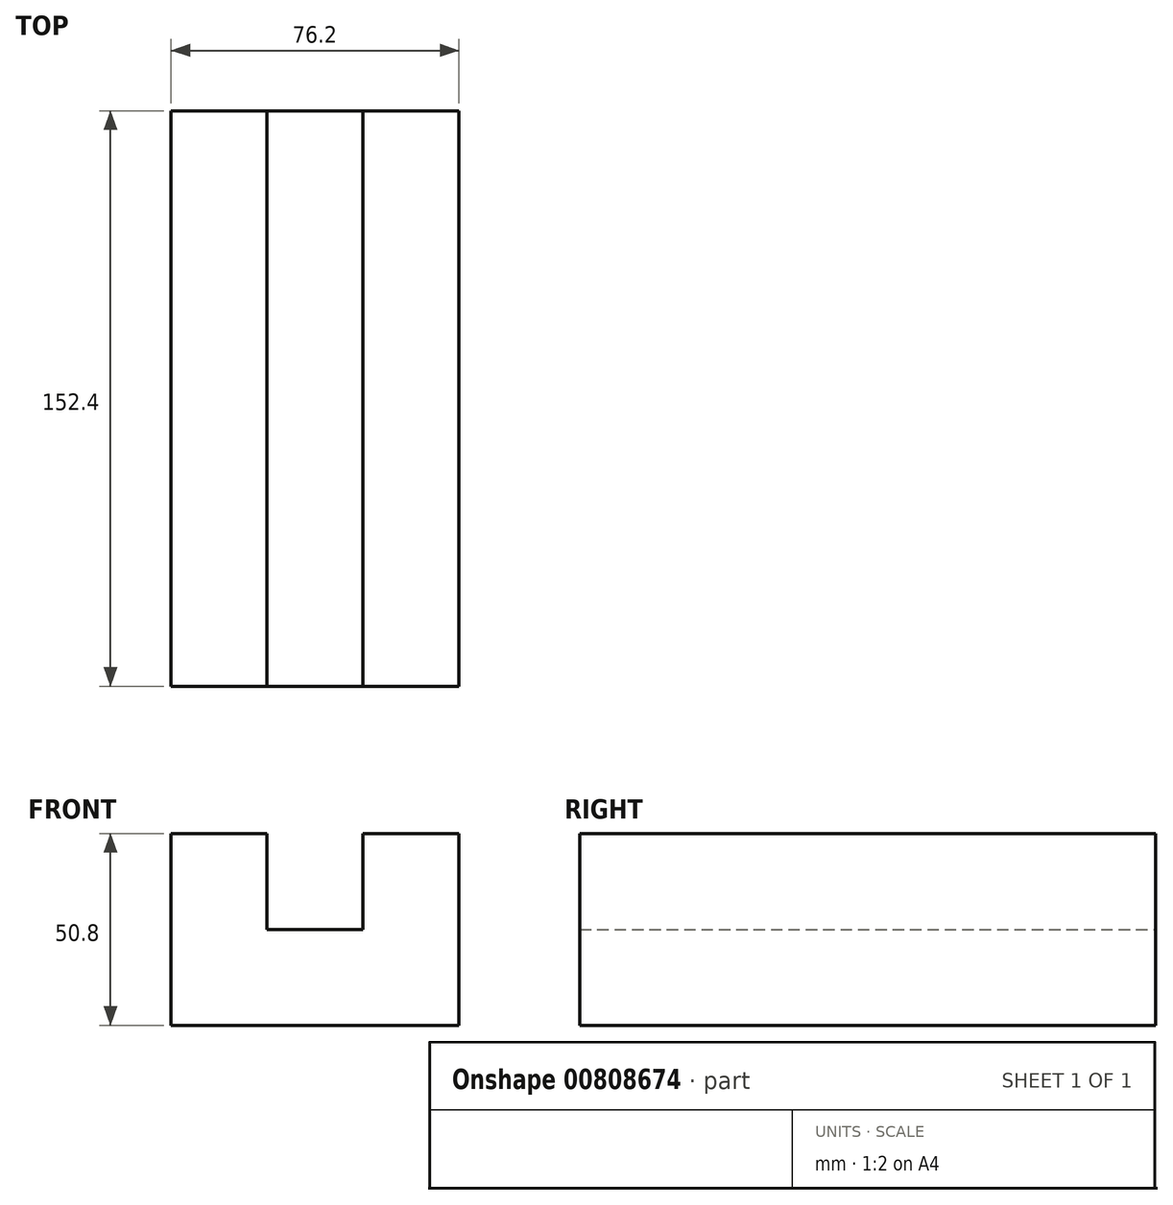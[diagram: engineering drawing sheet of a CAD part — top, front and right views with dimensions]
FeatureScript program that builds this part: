
annotation { "Feature Type Name" : "Feature", "Feature Type Description" : "" }
export const myFeature = defineFeature(function(context is Context, id is Id, definition is map)
    precondition{}
    {
        {
            var Q0;
            Q0=qCreatedBy(makeId("Front.planeOp"),FACE);
            var sketch = newSketch(context, id + "F0", { "sketchPlane" : qUnion([Q0])});
            skLineSegment(sketch, "E0", {"start": v(-76.2, 0) * mm, "end": v(0, 0) * mm});
            skLineSegment(sketch, "E1", {"start": v(0, 0) * mm, "end": v(0, 50.8) * mm});
            skLineSegment(sketch, "E2", {"start": v(-76.2, 0) * mm, "end": v(-76.2, 50.8) * mm});
            skLineSegment(sketch, "E3", {"start": v(-76.2, 50.8) * mm, "end": v(-50.8, 50.8) * mm});
            skLineSegment(sketch, "E4", {"start": v(-50.8, 50.8) * mm, "end": v(-50.8, 25.4) * mm});
            skLineSegment(sketch, "E5", {"start": v(-50.8, 25.4) * mm, "end": v(-25.4, 25.4) * mm});
            skLineSegment(sketch, "E6", {"start": v(-25.4, 25.4) * mm, "end": v(-25.4, 50.8) * mm});
            skLineSegment(sketch, "E7", {"start": v(-25.4, 50.8) * mm, "end": v(0, 50.8) * mm});
            skSolve(sketch);
        }
        {
            var Q0;
            Q0 = qSketchRegion(id + "F0", true);
            extrude(context, id + "F1", {"entities" : qUnion([Q0]), "depth" : 152.4 * mm, "offsetDistance" : 25.4 * mm});
        }
    });
